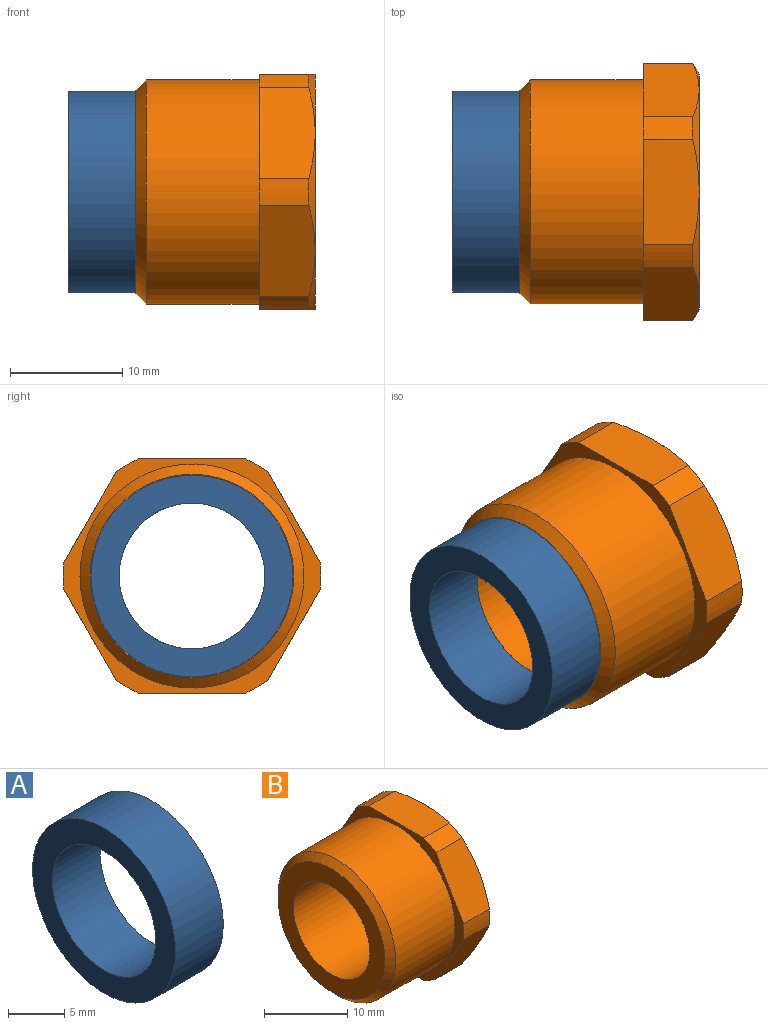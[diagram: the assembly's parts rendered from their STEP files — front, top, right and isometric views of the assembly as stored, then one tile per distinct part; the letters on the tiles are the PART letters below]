
ASSEMBLY  parts=2 mates=1
PART A: 4 faces, bbox 6x18x18 mm
  f0: cylinder r=9mm len=18mm, axis (1,0,0), area 339.3mm2, adj f2,f3
  f1: cylinder r=6.5mm len=13mm, axis (1,0,0), area 245mm2, adj f2,f3
  f2: plane 18x18mm, normal (-1,0,0), area 121.7mm2, adj f0,f1
  f3: plane 18x18mm, normal (1,0,0), area 121.7mm2, adj f0,f1
PART B: 24 faces, bbox 16x23x23 mm
  f0: cone r=9.54mm half-angle=45deg, axis (1,0,0), area 78mm2, adj f1,f23
  f1: cylinder r=10mm len=20mm, axis (-1,0,0), area 633.3mm2, adj f0,f13
  f2: cylinder r=6.5mm len=16mm, axis (-1,0,0), area 653.5mm2, adj f20,f23
  f3: cylinder r=11.5mm len=4.42mm, axis (-1,0,0), area 10.5mm2, adj f5,f8,f9,f13
  f4: cylinder r=11.5mm len=4.42mm, axis (-1,0,0), area 10.5mm2, adj f6,f11,f12,f13
  f5: cone r=11mm half-angle=60deg, axis (-1,0,0), area 6mm2, adj f3,f8,f9,f20
  f6: cone r=11mm half-angle=60deg, axis (-1,0,0), area 6mm2, adj f4,f11,f12,f20
  f7: plane 9.38x5mm, normal (0,0,1), area 45.1mm2, adj f13,f16,f19,f21,f22
  f8: plane 8.12x5mm, normal (0,-0.87,0.5), area 45.1mm2, adj f3,f5,f13,f21,f22
  f9: plane 8.12x5mm, normal (0,-0.87,-0.5), area 45.1mm2, adj f3,f5,f13,f15,f18
  f10: plane 9.38x5mm, normal (0,0,-1), area 45.1mm2, adj f13,f14,f15,f17,f18
  f11: plane 8.12x5mm, normal (0,0.87,-0.5), area 45.1mm2, adj f4,f6,f13,f14,f17
  f12: plane 8.12x5mm, normal (0,0.87,0.5), area 45.1mm2, adj f4,f6,f13,f16,f19
  f13: plane 23x21mm, normal (-1,0,0), area 63.5mm2, adj f1,f3,f4,f7,f8,f9,f10,f11
  f14: cone r=11mm half-angle=60deg, axis (-1,0,0), area 6mm2, adj f10,f11,f17,f20
  f15: cone r=11mm half-angle=60deg, axis (-1,0,0), area 6mm2, adj f9,f10,f18,f20
  f16: cone r=11mm half-angle=60deg, axis (-1,0,0), area 6mm2, adj f7,f12,f19,f20
  f17: cylinder r=11.5mm len=4.42mm, axis (-1,0,0), area 10.5mm2, adj f10,f11,f13,f14
  f18: cylinder r=11.5mm len=4.42mm, axis (-1,0,0), area 10.5mm2, adj f9,f10,f13,f15
  f19: cylinder r=11.5mm len=4.42mm, axis (-1,0,0), area 10.5mm2, adj f7,f12,f13,f16
  f20: plane 21x21mm, normal (1,0,0), area 213.6mm2, adj f2,f5,f6,f14,f15,f16,f21
  f21: cone r=11mm half-angle=60deg, axis (-1,0,0), area 6mm2, adj f7,f8,f20,f22
  f22: cylinder r=11.5mm len=4.42mm, axis (-1,0,0), area 10.5mm2, adj f7,f8,f13,f21
  f23: plane 18.16x18.16mm, normal (-1,0,0), area 126.3mm2, adj f0,f2
PLACE A t=(-16,0,0)mm
PLACE B t=(-16,0,0)mm
MATE fastened B.f0 <-> A.f0  axis (-1,0,0) through (-16,0,0)mm
